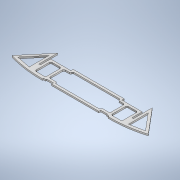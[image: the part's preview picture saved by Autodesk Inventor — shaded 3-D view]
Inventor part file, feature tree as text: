
AUTODESK INVENTOR PART (.ipt)
format: ipt  version: 2020.3 (Build 243373010, 373A)  size: 256,000 bytes
history: native  units: in
note: dims shown in document units (in); Inventor stores cm internally (conversion verified against a paired STEP export)
features: other x3, extrude x1, mirror x1, sketch x1
ambient origin geometry x8: Origin, YZ Plane, XZ Plane, XY Plane, X Axis, Y Axis, Z Axis, Center Point
bodies: Solid1 (feature_tree)
feature tree (6):
  other  "bulkhead_B1"
  other  "base_sketch.ipt"
  extrude  "Extrusion1"  Depth=0.0787in
  mirror  "Mirror1"
  other  "bulkhead_B1_plane"
  sketch  "Sketch2"  dims[d0=0.3937in d1=0.1181in d2=0.1181in d4=0.1181in d6=0.1181in d9=0.1181in d11=0.1181in d13=0.1181in d14=0.0787in d18=0.0787in d19=0.0in d20=0.1181in d21=0.0787in d22=0.0472in d23=0.0472in d24=0.2362in d25=0.2362in d26=0.1181in d28=0.0079in d29=0.0787in d33=0.1969in d34=0.7902in d35=0.0787in d36=0.0787in d37=0.7902in d38=0.1181in]
